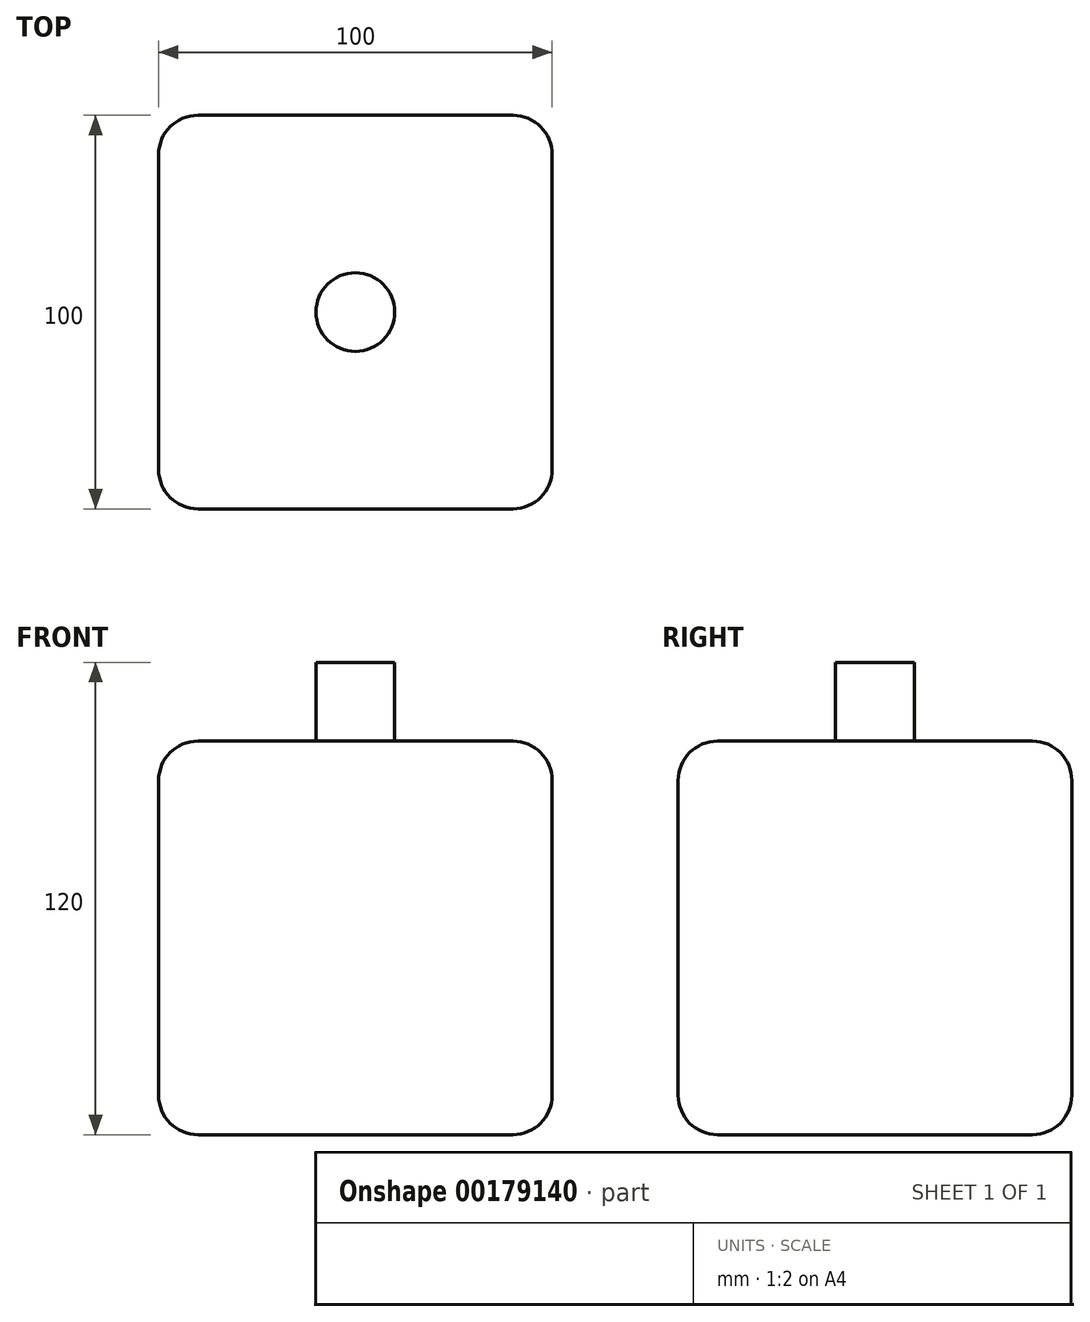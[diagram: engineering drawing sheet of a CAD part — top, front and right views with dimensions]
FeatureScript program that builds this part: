
annotation { "Feature Type Name" : "Feature", "Feature Type Description" : "" }
export const myFeature = defineFeature(function(context is Context, id is Id, definition is map)
    precondition{}
    {
        {
            var Q0;
            Q0=qCreatedBy(makeId("Top.planeOp"),FACE);
            var sketch = newSketch(context, id + "F0", { "sketchPlane" : qUnion([Q0])});
            skLineSegment(sketch, "E0", {"start": v(0, 0) * mm, "end": v(100, 0) * mm});
            skLineSegment(sketch, "E1", {"start": v(100, 0) * mm, "end": v(100, 100) * mm});
            skLineSegment(sketch, "E2", {"start": v(100, 100) * mm, "end": v(0, 100) * mm});
            skLineSegment(sketch, "E3", {"start": v(0, 100) * mm, "end": v(0, 0) * mm});
            skSolve(sketch);
        }
        {
            var Q0;
            Q0=makeQuery(id+"F0.imprint","IMPRINT",FACE,{"disambiguationData":[TD([[makeQuery(id+"F0.imprint","IMPRINT",EDGE,{"derivedFrom":sQuery(id+"F0.wireOp",EDGE,"E0")}),1.0]])]});
            extrude(context, id + "F1", {"entities" : qUnion([Q0]), "oppositeDirection" : true, "depth" : 100 * mm});
        }
        {
            var Q0;
            Q0=makeQuery(id+"F1.opExtrude","CAP_FACE",FACE,{"disambiguationData":[OSD([sQuery(id+"F0.wireOp",EDGE,"E0"),sQuery(id+"F0.wireOp",EDGE,"E1"),sQuery(id+"F0.wireOp",EDGE,"E2"),sQuery(id+"F0.wireOp",EDGE,"E3")])],"isStart":true});
            var sketch = newSketch(context, id + "F2", { "sketchPlane" : qUnion([Q0])});
            skLineSegment(sketch, "E4", {"start": v(0, 100) * mm, "end": v(100, 0) * mm, "construction": true});
            skLineSegment(sketch, "E5", {"start": v(100, 100) * mm, "end": v(0, 0) * mm, "construction": true});
            skLineSegment(sketch, "E6", {"start": v(50, 0) * mm, "end": v(50, 100) * mm, "construction": true});
            skCircle(sketch, "E7", {"center": v(50, 50) * mm, "radius": 10 * mm});
            skSolve(sketch);
        }
        {
            var Q0;
            Q0=makeQuery(id+"F2.imprint","IMPRINT",FACE,{"disambiguationData":[TD([[makeQuery(id+"F2.imprint","IMPRINT",EDGE,{"derivedFrom":sQuery(id+"F2.wireOp",EDGE,"E7")}),1.0]])]});
            extrude(context, id + "F3", {"entities" : qUnion([Q0]), "operationType" : NewBodyOperationType.ADD, "depth" : 20 * mm});
        }
        {
            var Q0;
            Q0=makeQuery(id+"F1.opExtrude","SWEPT_FACE",FACE,{"disambiguationData":[OSD([sQuery(id+"F0.wireOp",EDGE,"E0")])]});
            var Q1;
            Q1=makeQuery(id+"F1.opExtrude","CAP_EDGE",EDGE,{"disambiguationData":[OSD([sQuery(id+"F0.wireOp",EDGE,"E1")])],"isStart":true});
            var Q2;
            Q2=makeQuery(id+"F1.opExtrude","SWEPT_EDGE",EDGE,{"disambiguationData":[OSD([sQuery(id+"F0.wireOp",EDGE,"E1"),sQuery(id+"F0.wireOp",EDGE,"E2")])]});
            var Q3;
            Q3=makeQuery(id+"F1.opExtrude","CAP_EDGE",EDGE,{"disambiguationData":[OSD([sQuery(id+"F0.wireOp",EDGE,"E2")])],"isStart":true});
            var Q4;
            Q4=makeQuery(id+"F1.opExtrude","CAP_EDGE",EDGE,{"disambiguationData":[OSD([sQuery(id+"F0.wireOp",EDGE,"E3")])],"isStart":true});
            var Q5;
            Q5=makeQuery(id+"F1.opExtrude","CAP_EDGE",EDGE,{"disambiguationData":[OSD([sQuery(id+"F0.wireOp",EDGE,"E2")])],"isStart":false});
            var Q6;
            Q6=makeQuery(id+"F1.opExtrude","SWEPT_EDGE",EDGE,{"disambiguationData":[OSD([sQuery(id+"F0.wireOp",EDGE,"E2"),sQuery(id+"F0.wireOp",EDGE,"E3")])]});
            var Q7;
            Q7=makeQuery(id+"F1.opExtrude","CAP_EDGE",EDGE,{"disambiguationData":[OSD([sQuery(id+"F0.wireOp",EDGE,"E3")])],"isStart":false});
            var Q8;
            Q8=makeQuery(id+"F1.opExtrude","CAP_EDGE",EDGE,{"disambiguationData":[OSD([sQuery(id+"F0.wireOp",EDGE,"E1")])],"isStart":false});
            fillet(context, id + "F4", {"entities" : qUnion([Q0, Q1, Q2, Q3, Q4, Q5, Q6, Q7, Q8]), "radius" : 10 * mm, "tangentPropagation" : true, "allowEdgeOverflow" : false});
        }
    });
